# Revit family: Haworth_Pergola_Panel_TopRail_Straight
name_source: partatom
category: Furniture Systems
revit_build: Autodesk Revit 2018 (Build: 20170223_1515(x64)
units: mm (PartAtom-declared; Revit-internal decimal feet)

## family parameters
Always vertical = Yes
Cut with Voids When Loaded = No
OmniClass Number = 23.40.70.14.64.21
OmniClass Title = Systems Furniture
Part Type = Normal
Room Calculation Point = No
Round Connector Dimension = Use Diameter
Shared = No
Work Plane-Based = No

## types (5) — shared parameters
Actual Depth = 4"
Actual Height = 4 25/128"
Assembly Code = E2020200
Description = Haworth - Pergola Panel - Top Rail - Straight
Manufacturer = Haworth
Max. Height = 4"
Max. Width = 144"
Min. Height = 4"
Min. Width = 48"
Model = Haworth Pergola
Revision Number = 1
Size = Verify Final Dim. w/ Haworth
Standard Width = 48,  72, 96, 120, and 144 in.
Sustainability Info = http://www.haworth.com
Trim Finish = Haworth _ Paint _ Undecided _ Pergola
URL = http://www.haworth.com
URL - Product = https://www.haworth.com
Warranty = http://www.haworth.com

## per-type parameters (varying)
| type | Actual Width | Width |
| 48w | 48" | 48" |
| 72w | 72" | 72" |
| 96w | 96" | 96" |
| 120w | 120" | 120" |
| 144w | 144" | 144" |

## geometry (parser evidence)
native form markers: Sweep x3
no freeform markers — native parametric forms only
